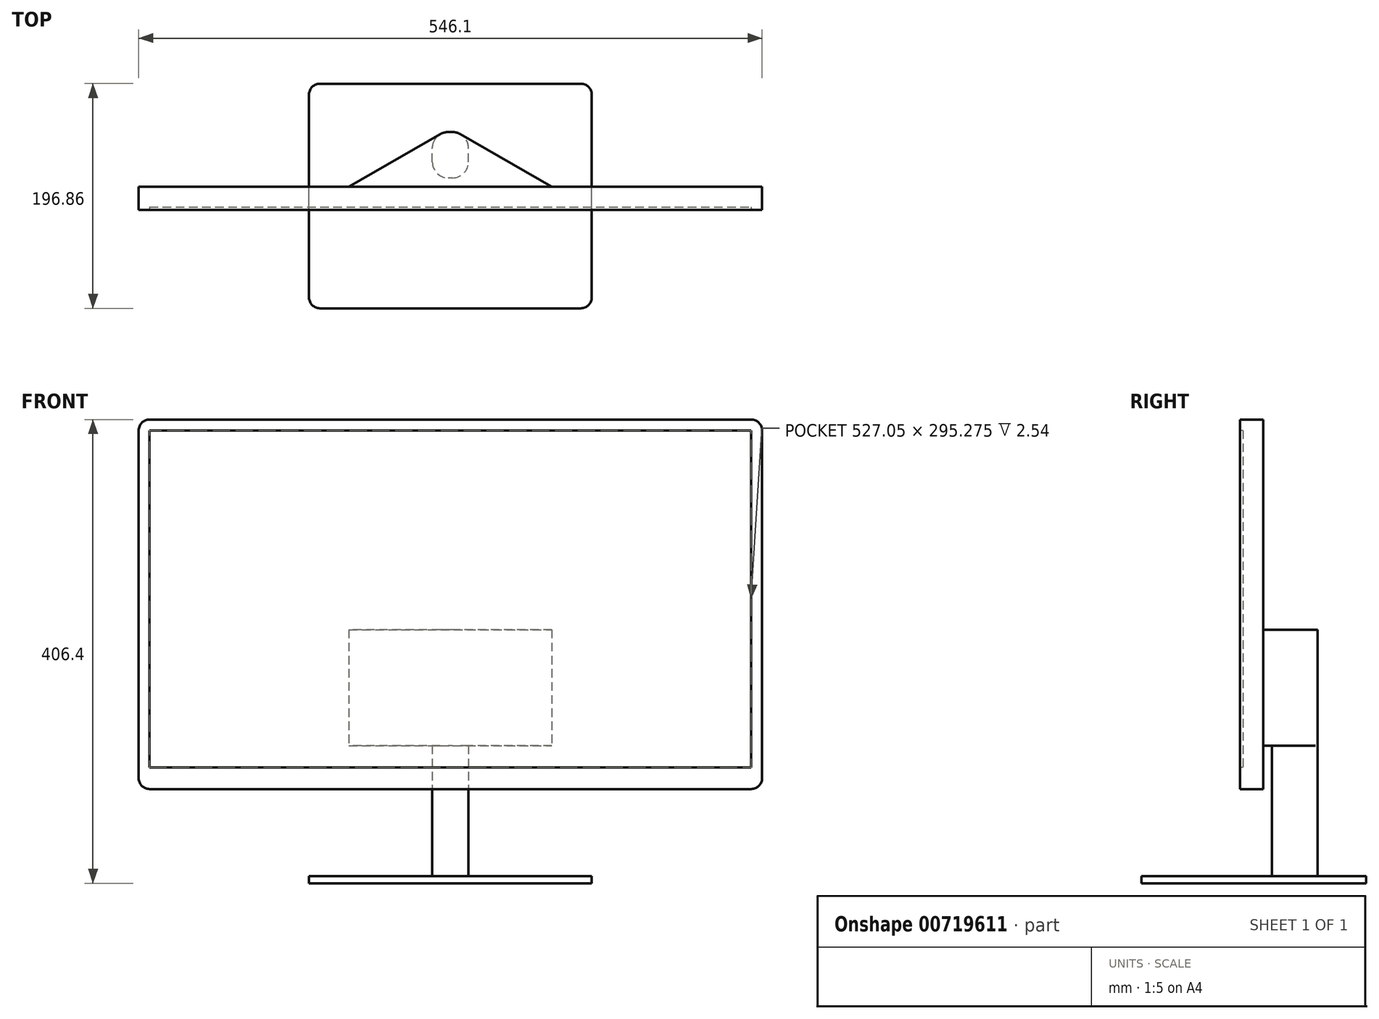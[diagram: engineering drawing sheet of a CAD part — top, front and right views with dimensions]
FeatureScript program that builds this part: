
annotation { "Feature Type Name" : "Feature", "Feature Type Description" : "" }
export const myFeature = defineFeature(function(context is Context, id is Id, definition is map)
    precondition{}
    {
        {
            var Q0;
            Q0=qCreatedBy(makeId("Top.planeOp"),FACE);
            var sketch = newSketch(context, id + "F0", { "sketchPlane" : qUnion([Q0])});
            skLineSegment(sketch, "E0.bottom", {"start": v(114.3, -98.42) * mm, "end": v(-114.3, -98.42) * mm});
            skLineSegment(sketch, "E0.top", {"start": v(114.3, 98.43) * mm, "end": v(-114.3, 98.43) * mm});
            skLineSegment(sketch, "E0.left", {"start": v(123.83, -88.9) * mm, "end": v(123.82, 88.9) * mm});
            skLineSegment(sketch, "E0.right", {"start": v(-123.83, -88.9) * mm, "end": v(-123.83, 88.9) * mm});
            skPoint(sketch, "E0.middle", {"position": v(0, 0) * mm});
            skPoint(sketch, "E1.visualSharp", {"position": v(-123.83, 98.43) * mm});
            skArc(sketch, "E1.filletArc", {"start": v(-114.3, 98.42) * mm, "mid": v(-121.04, 95.64) * mm, "end": v(-123.83, 88.9) * mm});
            skPoint(sketch, "E2.visualSharp", {"position": v(-123.83, -98.42) * mm});
            skArc(sketch, "E2.filletArc", {"start": v(-123.83, -88.9) * mm, "mid": v(-121.04, -95.64) * mm, "end": v(-114.3, -98.42) * mm});
            skPoint(sketch, "E3.visualSharp", {"position": v(123.83, -98.42) * mm});
            skArc(sketch, "E3.filletArc", {"start": v(114.3, -98.42) * mm, "mid": v(121.04, -95.64) * mm, "end": v(123.83, -88.9) * mm});
            skPoint(sketch, "E4.visualSharp", {"position": v(123.82, 98.43) * mm});
            skArc(sketch, "E4.filletArc", {"start": v(123.82, 88.9) * mm, "mid": v(121.04, 95.64) * mm, "end": v(114.3, 98.43) * mm});
            skSolve(sketch);
        }
        {
            var Q0;
            Q0=makeQuery(id+"F0.imprint","IMPRINT",FACE,{"disambiguationData":[TD([[makeQuery(id+"F0.imprint","IMPRINT",EDGE,{"derivedFrom":sQuery(id+"F0.wireOp",EDGE,"E0.bottom")}),-1.0]])]});
            extrude(context, id + "F1", {"entities" : qUnion([Q0]), "depth" : 6.35 * mm, "offsetDistance" : 25.4 * mm});
        }
        {
            var Q0;
            Q0=makeQuery(id+"F1.opExtrude","CAP_FACE",FACE,{"disambiguationData":[OSD([sQuery(id+"F0.wireOp",EDGE,"E0.bottom"),sQuery(id+"F0.wireOp",EDGE,"E0.top"),sQuery(id+"F0.wireOp",EDGE,"E0.left"),sQuery(id+"F0.wireOp",EDGE,"E0.right"),sQuery(id+"F0.wireOp",EDGE,"E1.filletArc"),sQuery(id+"F0.wireOp",EDGE,"E2.filletArc"),sQuery(id+"F0.wireOp",EDGE,"E3.filletArc"),sQuery(id+"F0.wireOp",EDGE,"E4.filletArc")])],"isStart":false});
            var sketch = newSketch(context, id + "F2", { "sketchPlane" : qUnion([Q0])});
            skLineSegment(sketch, "E5", {"start": v(0, 98.43) * mm, "end": v(0, -98.42) * mm, "construction": true});
            skLineSegment(sketch, "E6.bottom", {"start": v(1.9, 15.88) * mm, "end": v(-1.9, 15.88) * mm});
            skLineSegment(sketch, "E6.top", {"start": v(1.9, 56) * mm, "end": v(-1.9, 56) * mm});
            skLineSegment(sketch, "E6.left", {"start": v(15.87, 29.85) * mm, "end": v(15.87, 42.04) * mm});
            skLineSegment(sketch, "E6.right", {"start": v(-15.88, 29.85) * mm, "end": v(-15.88, 42.04) * mm});
            skPoint(sketch, "E6.middle", {"position": v(0, 35.94) * mm});
            skPoint(sketch, "E7.visualSharp", {"position": v(-15.88, 15.88) * mm});
            skArc(sketch, "E7.filletArc", {"start": v(-15.88, 29.85) * mm, "mid": v(-11.78, 19.97) * mm, "end": v(-1.9, 15.88) * mm});
            skPoint(sketch, "E8.visualSharp", {"position": v(-15.88, 56) * mm});
            skArc(sketch, "E8.filletArc", {"start": v(-1.9, 56) * mm, "mid": v(-11.78, 51.92) * mm, "end": v(-15.88, 42.04) * mm});
            skPoint(sketch, "E9.visualSharp", {"position": v(15.87, 56) * mm});
            skArc(sketch, "E9.filletArc", {"start": v(15.87, 42.04) * mm, "mid": v(11.78, 51.92) * mm, "end": v(1.9, 56) * mm});
            skPoint(sketch, "E10.visualSharp", {"position": v(15.87, 15.88) * mm});
            skArc(sketch, "E10.filletArc", {"start": v(1.9, 15.88) * mm, "mid": v(11.78, 19.97) * mm, "end": v(15.87, 29.85) * mm});
            skSolve(sketch);
        }
        {
            var Q0;
            Q0=makeQuery(id+"F2.imprint","IMPRINT",FACE,{"disambiguationData":[TD([[makeQuery(id+"F2.imprint","IMPRINT",EDGE,{"derivedFrom":sQuery(id+"F2.wireOp",EDGE,"E6.bottom")}),-1.0]])]});
            extrude(context, id + "F3", {"entities" : qUnion([Q0]), "operationType" : NewBodyOperationType.ADD, "depth" : 114.3 * mm, "offsetDistance" : 25.4 * mm});
        }
        {
            var Q0;
            Q0=makeQuery(id+"F3.opExtrude","CAP_FACE",FACE,{"disambiguationData":[OSD([sQuery(id+"F2.wireOp",EDGE,"E6.bottom"),sQuery(id+"F2.wireOp",EDGE,"E6.top"),sQuery(id+"F2.wireOp",EDGE,"E6.left"),sQuery(id+"F2.wireOp",EDGE,"E6.right"),sQuery(id+"F2.wireOp",EDGE,"E7.filletArc"),sQuery(id+"F2.wireOp",EDGE,"E8.filletArc"),sQuery(id+"F2.wireOp",EDGE,"E9.filletArc"),sQuery(id+"F2.wireOp",EDGE,"E10.filletArc")])],"isStart":false});
            var sketch = newSketch(context, id + "F4", { "sketchPlane" : qUnion([Q0])});
            skLineSegment(sketch, "E11", {"start": v(-8.85, 54.16) * mm, "end": v(-88.9, 8.26) * mm});
            skLineSegment(sketch, "E12", {"start": v(-88.9, 8.26) * mm, "end": v(88.9, 8.26) * mm});
            skLineSegment(sketch, "E13", {"start": v(88.9, 8.26) * mm, "end": v(8.85, 54.16) * mm});
            skSolve(sketch);
        }
        {
            var Q0;
            Q0 = qSketchRegion(id + "F4", true);
            var Q1;
            {var subQ3=sQuery(id+"F4.wireOp",EDGE,"E11");Q1=makeQuery(id+"F4.imprint","IMPRINT",FACE,{"disambiguationData":[TD([[makeQuery(id+"F4.imprint","IMPRINT",EDGE,{"derivedFrom":subQ3}),1.0]])]});}
            var Q2;
            Q2=makeQuery(id+"F4.imprint","IMPRINT",FACE,{"disambiguationData":[TD([[makeQuery(id+"F4.imprint","IMPRINT",EDGE,{"derivedFrom":makeQuery(id+"F3.opExtrude","CAP_EDGE",EDGE,{"disambiguationData":[OSD([sQuery(id+"F2.wireOp",EDGE,"E6.bottom")])],"isStart":false})}),-1.0]])]});
            extrude(context, id + "F5", {"entities" : qUnion([Q0, Q1, Q2]), "operationType" : NewBodyOperationType.ADD, "depth" : 101.6 * mm, "offsetDistance" : 25.4 * mm});
        }
        {
            var Q0;
            Q0=makeQuery(id+"F5.opExtrude","SWEPT_FACE",FACE,{"disambiguationData":[OSD([sQuery(id+"F4.wireOp",EDGE,"E12")])]});
            var sketch = newSketch(context, id + "F6", { "sketchPlane" : qUnion([Q0])});
            skLineSegment(sketch, "E14.bottom", {"start": v(-263.53, 406.4) * mm, "end": v(263.53, 406.4) * mm});
            skLineSegment(sketch, "E14.top", {"start": v(-263.53, 82.55) * mm, "end": v(263.53, 82.55) * mm});
            skLineSegment(sketch, "E14.left", {"start": v(-273.05, 396.88) * mm, "end": v(-273.05, 92.08) * mm});
            skLineSegment(sketch, "E14.right", {"start": v(273.05, 396.88) * mm, "end": v(273.05, 92.08) * mm});
            skLineSegment(sketch, "E15", {"start": v(0, 406.4) * mm, "end": v(0, 82.55) * mm, "construction": true});
            skPoint(sketch, "E16.visualSharp", {"position": v(-273.05, 406.4) * mm});
            skArc(sketch, "E16.filletArc", {"start": v(-263.53, 406.4) * mm, "mid": v(-270.26, 403.61) * mm, "end": v(-273.05, 396.88) * mm});
            skPoint(sketch, "E17.visualSharp", {"position": v(-273.05, 82.55) * mm});
            skArc(sketch, "E17.filletArc", {"start": v(-273.05, 92.08) * mm, "mid": v(-270.26, 85.34) * mm, "end": v(-263.53, 82.55) * mm});
            skPoint(sketch, "E18.visualSharp", {"position": v(273.05, 82.55) * mm});
            skArc(sketch, "E18.filletArc", {"start": v(263.53, 82.55) * mm, "mid": v(270.26, 85.34) * mm, "end": v(273.05, 92.08) * mm});
            skPoint(sketch, "E19.visualSharp", {"position": v(273.05, 406.4) * mm});
            skArc(sketch, "E19.filletArc", {"start": v(273.05, 396.88) * mm, "mid": v(270.26, 403.61) * mm, "end": v(263.53, 406.4) * mm});
            skSolve(sketch);
        }
        {
            var Q0;
            Q0 = qSketchRegion(id + "F6", true);
            extrude(context, id + "F7", {"entities" : qUnion([Q0]), "operationType" : NewBodyOperationType.ADD, "depth" : 20.32 * mm, "offsetDistance" : 25.4 * mm});
        }
        {
            var Q0;
            Q0=makeQuery(id+"F7.opExtrude","CAP_FACE",FACE,{"disambiguationData":[OSD([sQuery(id+"F6.wireOp",EDGE,"E14.bottom"),sQuery(id+"F6.wireOp",EDGE,"E14.top"),sQuery(id+"F6.wireOp",EDGE,"E14.left"),sQuery(id+"F6.wireOp",EDGE,"E14.right"),sQuery(id+"F6.wireOp",EDGE,"E16.filletArc"),sQuery(id+"F6.wireOp",EDGE,"E17.filletArc"),sQuery(id+"F6.wireOp",EDGE,"E18.filletArc"),sQuery(id+"F6.wireOp",EDGE,"E19.filletArc")])],"isStart":false});
            var sketch = newSketch(context, id + "F8", { "sketchPlane" : qUnion([Q0])});
            skLineSegment(sketch, "E20.bottom", {"start": v(-263.53, 396.88) * mm, "end": v(263.53, 396.88) * mm});
            skLineSegment(sketch, "E20.top", {"start": v(-263.53, 101.6) * mm, "end": v(263.53, 101.6) * mm});
            skLineSegment(sketch, "E20.left", {"start": v(-263.53, 396.88) * mm, "end": v(-263.53, 101.6) * mm});
            skLineSegment(sketch, "E20.right", {"start": v(263.53, 396.88) * mm, "end": v(263.53, 101.6) * mm});
            skLineSegment(sketch, "E21", {"start": v(0, 406.4) * mm, "end": v(0, 82.55) * mm, "construction": true});
            skSolve(sketch);
        }
        {
            var Q0;
            Q0 = qSketchRegion(id + "F8", true);
            extrude(context, id + "F9", {"entities" : qUnion([Q0]), "operationType" : NewBodyOperationType.REMOVE, "oppositeDirection" : true, "depth" : 2.54 * mm, "offsetDistance" : 25.4 * mm});
        }
    });
